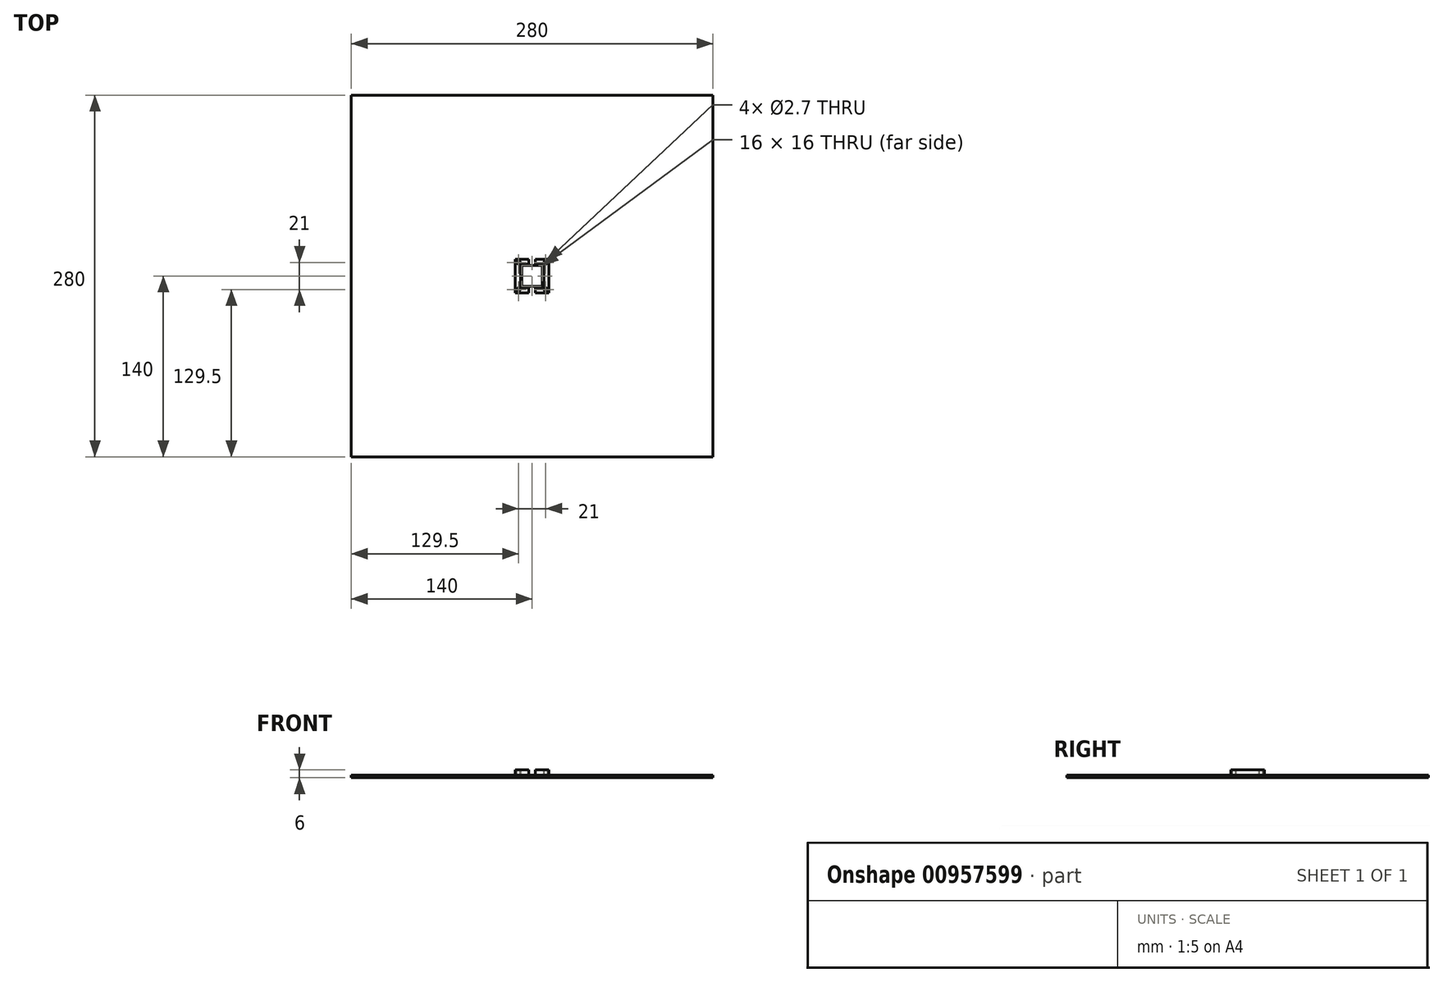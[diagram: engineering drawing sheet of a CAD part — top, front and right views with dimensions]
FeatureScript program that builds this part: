
annotation { "Feature Type Name" : "Feature", "Feature Type Description" : "" }
export const myFeature = defineFeature(function(context is Context, id is Id, definition is map)
    precondition{}
    {
        {
            var Q0;
            Q0=qCreatedBy(makeId("Top.planeOp"),FACE);
            var sketch = newSketch(context, id + "F0", { "sketchPlane" : qUnion([Q0])});
            skLineSegment(sketch, "E0.bottom", {"start": v(25, 25) * mm, "end": v(-25, 25) * mm});
            skLineSegment(sketch, "E0.top", {"start": v(25, -25) * mm, "end": v(-25, -25) * mm});
            skLineSegment(sketch, "E0.left", {"start": v(25, 25) * mm, "end": v(25, -25) * mm});
            skLineSegment(sketch, "E0.right", {"start": v(-25, 25) * mm, "end": v(-25, -25) * mm});
            skPoint(sketch, "E0.middle", {"position": v(0, 0) * mm});
            skLineSegment(sketch, "E1.bottom", {"start": v(140, -140) * mm, "end": v(-140, -140) * mm});
            skLineSegment(sketch, "E1.top", {"start": v(140, 140) * mm, "end": v(-140, 140) * mm});
            skLineSegment(sketch, "E1.left", {"start": v(140, -140) * mm, "end": v(140, 140) * mm});
            skLineSegment(sketch, "E1.right", {"start": v(-140, -140) * mm, "end": v(-140, 140) * mm});
            skSolve(sketch);
        }
        {
            var Q0;
            Q0=makeQuery(id+"F0.imprint","IMPRINT",FACE,{"disambiguationData":[TD([[makeQuery(id+"F0.imprint","IMPRINT",EDGE,{"derivedFrom":sQuery(id+"F0.wireOp",EDGE,"E0.bottom")}),-1.0]])]});
            extrude(context, id + "F1", {"entities" : qUnion([Q0]), "depth" : 18 * mm, "offsetDistance" : 25 * mm});
        }
        {
            var Q0;
            Q0=makeQuery(id+"F0.imprint","IMPRINT",FACE,{"disambiguationData":[TD([[makeQuery(id+"F0.imprint","IMPRINT",EDGE,{"derivedFrom":sQuery(id+"F0.wireOp",EDGE,"E0.bottom")}),-1.0]])]});
            var Q1;
            Q1=makeQuery(id+"F0.imprint","IMPRINT",FACE,{"disambiguationData":[TD([[makeQuery(id+"F0.imprint","IMPRINT",EDGE,{"derivedFrom":sQuery(id+"F0.wireOp",EDGE,"E0.bottom")}),1.0]])]});
            extrude(context, id + "F2", {"entities" : qUnion([Q0, Q1]), "operationType" : NewBodyOperationType.ADD, "oppositeDirection" : true, "depth" : 2 * mm, "offsetDistance" : 25 * mm});
        }
        {
            var Q0;
            {var subQ0=sQuery(id+"F0.wireOp",EDGE,"E1.left");Q0=makeQuery(id+"F2.boolean.opBoolean","MERGE",FACE,{"derivedFrom":[makeQuery(id+"F1.opExtrude","SWEPT_FACE",FACE,{"disambiguationData":[OSD([subQ0])]}),makeQuery(id+"F2.opExtrude","SWEPT_FACE",FACE,{"disambiguationData":[OSD([subQ0])]})]});}
            var sketch = newSketch(context, id + "F3", { "sketchPlane" : qUnion([Q0])});
            skLineSegment(sketch, "E2.bottom", {"start": v(-7.98, 6) * mm, "end": v(8.02, 6) * mm});
            skLineSegment(sketch, "E2.top", {"start": v(-7.98, 0) * mm, "end": v(8.02, 0) * mm});
            skLineSegment(sketch, "E2.left", {"start": v(-7.98, 6) * mm, "end": v(-7.98, 0) * mm});
            skLineSegment(sketch, "E2.right", {"start": v(8.02, 6) * mm, "end": v(8.02, 0) * mm});
            skLineSegment(sketch, "E3", {"start": v(-7.98, -2) * mm, "end": v(-7.98, 8) * mm, "construction": true});
            skLineSegment(sketch, "E4", {"start": v(8.02, -2) * mm, "end": v(8.02, 8) * mm, "construction": true});
            skLineSegment(sketch, "E5", {"start": v(-140, 6) * mm, "end": v(-7.98, 6) * mm, "construction": true});
            skLineSegment(sketch, "E6", {"start": v(8.02, 6) * mm, "end": v(140, 6) * mm, "construction": true});
            skSolve(sketch);
        }
        {
            var Q0;
            Q0=makeQuery(id+"F3.imprint","IMPRINT",FACE,{"disambiguationData":[TD([[makeQuery(id+"F3.imprint","IMPRINT",EDGE,{"derivedFrom":sQuery(id+"F3.wireOp",EDGE,"E2.bottom")}),-1.0]])]});
            extrude(context, id + "F4", {"entities" : qUnion([Q0]), "operationType" : NewBodyOperationType.REMOVE, "endBound" : BoundingType.UP_TO_NEXT, "oppositeDirection" : true, "depth" : 25 * mm, "offsetDistance" : 25 * mm});
        }
        {
            var Q0;
            Q0=makeQuery(id+"F1.opExtrude","CAP_FACE",FACE,{"disambiguationData":[OSD([sQuery(id+"F0.wireOp",EDGE,"E0.bottom"),sQuery(id+"F0.wireOp",EDGE,"E0.top"),sQuery(id+"F0.wireOp",EDGE,"E0.left"),sQuery(id+"F0.wireOp",EDGE,"E0.right"),sQuery(id+"F0.wireOp",EDGE,"E1.bottom"),sQuery(id+"F0.wireOp",EDGE,"E1.top"),sQuery(id+"F0.wireOp",EDGE,"E1.left"),sQuery(id+"F0.wireOp",EDGE,"E1.right")])],"isStart":false});
            var sketch = newSketch(context, id + "F5", { "sketchPlane" : qUnion([Q0])});
            skLineSegment(sketch, "E7.bottom", {"start": v(-140, -140) * mm, "end": v(140, -140) * mm});
            skLineSegment(sketch, "E7.top", {"start": v(-140, 140) * mm, "end": v(140, 140) * mm});
            skLineSegment(sketch, "E7.left", {"start": v(-140, -140) * mm, "end": v(-140, 140) * mm});
            skLineSegment(sketch, "E7.right", {"start": v(140, -140) * mm, "end": v(140, 140) * mm});
            skLineSegment(sketch, "E8.bottom", {"start": v(8, -8) * mm, "end": v(-8, -8) * mm});
            skLineSegment(sketch, "E8.top", {"start": v(8, 8) * mm, "end": v(-8, 8) * mm});
            skLineSegment(sketch, "E8.left", {"start": v(8, -8) * mm, "end": v(8, 8) * mm});
            skLineSegment(sketch, "E8.right", {"start": v(-8, -8) * mm, "end": v(-8, 8) * mm});
            skPoint(sketch, "E8.middle", {"position": v(0, 0) * mm});
            skSolve(sketch);
        }
        {
            var Q0;
            Q0=makeQuery(id+"F5.imprint","IMPRINT",FACE,{"disambiguationData":[TD([[makeQuery(id+"F5.imprint","IMPRINT",EDGE,{"derivedFrom":sQuery(id+"F5.wireOp",EDGE,"E8.bottom")}),1.0]])]});
            var Q1;
            Q1=makeQuery(id+"F5.imprint","IMPRINT",FACE,{"disambiguationData":[TD([[makeQuery(id+"F5.imprint","IMPRINT",EDGE,{"derivedFrom":sQuery(id+"F5.wireOp",EDGE,"E7.bottom")}),-1.0]])]});
            extrude(context, id + "F6", {"entities" : qUnion([Q0, Q1]), "depth" : 2 * mm, "offsetDistance" : 25 * mm});
        }
        {
            var Q0;
            Q0=makeQuery(id+"F6.opExtrude","CAP_FACE",FACE,{"disambiguationData":[OSD([sQuery(id+"F5.wireOp",EDGE,"E7.bottom"),sQuery(id+"F5.wireOp",EDGE,"E7.top"),sQuery(id+"F5.wireOp",EDGE,"E7.left"),sQuery(id+"F5.wireOp",EDGE,"E7.right"),sQuery(id+"F5.wireOp",EDGE,"E8.bottom"),sQuery(id+"F5.wireOp",EDGE,"E8.top"),sQuery(id+"F5.wireOp",EDGE,"E8.left"),sQuery(id+"F5.wireOp",EDGE,"E8.right")])],"isStart":false});
            var sketch = newSketch(context, id + "F7", { "sketchPlane" : qUnion([Q0])});
            skLineSegment(sketch, "E9.bottom", {"start": v(-9, 9) * mm, "end": v(9, 9) * mm});
            skLineSegment(sketch, "E9.top", {"start": v(-9, -9) * mm, "end": v(9, -9) * mm});
            skLineSegment(sketch, "E9.left", {"start": v(-9, 9) * mm, "end": v(-9, -9) * mm});
            skLineSegment(sketch, "E9.right", {"start": v(9, 9) * mm, "end": v(9, -9) * mm});
            skPoint(sketch, "E9.middle", {"position": v(0, 0) * mm});
            skLineSegment(sketch, "E10.bottom", {"start": v(13, 13) * mm, "end": v(-13, 13) * mm});
            skLineSegment(sketch, "E10.top", {"start": v(13, -13) * mm, "end": v(-13, -13) * mm});
            skLineSegment(sketch, "E10.left", {"start": v(13, 13) * mm, "end": v(13, -13) * mm});
            skLineSegment(sketch, "E10.right", {"start": v(-13, 13) * mm, "end": v(-13, -13) * mm});
            skSolve(sketch);
        }
        {
            var Q0;
            Q0=makeQuery(id+"F7.imprint","IMPRINT",FACE,{"disambiguationData":[TD([[makeQuery(id+"F7.imprint","IMPRINT",EDGE,{"derivedFrom":sQuery(id+"F7.wireOp",EDGE,"E9.bottom")}),1.0]])]});
            extrude(context, id + "F8", {"entities" : qUnion([Q0]), "operationType" : NewBodyOperationType.ADD, "depth" : 4 * mm, "offsetDistance" : 25 * mm});
        }
        {
            var Q0;
            Q0=makeQuery(id+"F8.opExtrude","CAP_FACE",FACE,{"disambiguationData":[OSD([sQuery(id+"F7.wireOp",EDGE,"E9.bottom"),sQuery(id+"F7.wireOp",EDGE,"E9.top"),sQuery(id+"F7.wireOp",EDGE,"E9.left"),sQuery(id+"F7.wireOp",EDGE,"E9.right"),sQuery(id+"F7.wireOp",EDGE,"E10.bottom"),sQuery(id+"F7.wireOp",EDGE,"E10.top"),sQuery(id+"F7.wireOp",EDGE,"E10.left"),sQuery(id+"F7.wireOp",EDGE,"E10.right")])],"isStart":false});
            var sketch = newSketch(context, id + "F9", { "sketchPlane" : qUnion([Q0])});
            skLineSegment(sketch, "E11", {"start": v(-2.5, 13) * mm, "end": v(-2.5, 9) * mm});
            skLineSegment(sketch, "E12.MirrorCS", {"start": v(2.5, 13) * mm, "end": v(2.5, 9) * mm});
            skLineSegment(sketch, "E13.MirrorCS", {"start": v(2.5, -13) * mm, "end": v(2.5, -9) * mm});
            skLineSegment(sketch, "E14.MirrorCS", {"start": v(-2.5, -13) * mm, "end": v(-2.5, -9) * mm});
            skLineSegment(sketch, "E15", {"start": v(-13, 13) * mm, "end": v(-9, 9) * mm, "construction": true});
            skPoint(sketch, "E16", {"position": v(-10.5, 10.5) * mm});
            skPoint(sketch, "E17.MirrorP", {"position": v(10.5, 10.5) * mm});
            skLineSegment(sketch, "E18.MirrorCS", {"start": v(13, 13) * mm, "end": v(9, 9) * mm, "construction": true});
            skLineSegment(sketch, "E19.MirrorCS", {"start": v(-13, -13) * mm, "end": v(-9, -9) * mm, "construction": true});
            skPoint(sketch, "E20.MirrorP", {"position": v(-10.5, -10.5) * mm});
            skLineSegment(sketch, "E21.MirrorCS", {"start": v(13, -13) * mm, "end": v(9, -9) * mm, "construction": true});
            skPoint(sketch, "E22.MirrorP", {"position": v(10.5, -10.5) * mm});
            skSolve(sketch);
        }
        {
            var Q0;
            Q0=sQuery(id+"F9.wireOp",VERTEX,"E16");
            var Q1;
            Q1=sQuery(id+"F9.wireOp",VERTEX,"E17.MirrorP");
            var Q2;
            Q2=sQuery(id+"F9.wireOp",VERTEX,"E20.MirrorP");
            var Q3;
            Q3=sQuery(id+"F9.wireOp",VERTEX,"E22.MirrorP");
            var Q4;
            Q4=makeQuery(id+"F6.opExtrude","SWEPT_BODY",BODY,{"disambiguationData":[OSD([sQuery(id+"F5.wireOp",EDGE,"E7.bottom"),sQuery(id+"F5.wireOp",EDGE,"E7.top"),sQuery(id+"F5.wireOp",EDGE,"E7.left"),sQuery(id+"F5.wireOp",EDGE,"E7.right"),sQuery(id+"F5.wireOp",EDGE,"E8.bottom"),sQuery(id+"F5.wireOp",EDGE,"E8.top"),sQuery(id+"F5.wireOp",EDGE,"E8.left"),sQuery(id+"F5.wireOp",EDGE,"E8.right")])]});
            hole(context, id + "F10", {"style" : HoleStyle.SIMPLE, "endStyle" : HoleEndStyle.BLIND, "standardTappedOrClearance" : lookupTablePath({ "standard" : "ISO", "engagement" : "50%", "pitch" : "0.5 mm", "size" : "M3", "type" : "Tapped" }), "standardBlindInLast" : lookupTablePath({ "standard" : "ISO", "fit" : "Normal", "engagement" : "50%", "pitch" : "0.5 mm", "size" : "M3", "type" : "Clearance & tapped" }), "holeDiameter" : 2.7 * mm, "majorDiameter" : 3 * mm, "showTappedDepth" : true, "holeDepth" : 8 * mm, "isTappedThrough" : true, "tappedDepth" : 6.5 * mm, "tapClearance" : 3, "locations" : qUnion([Q0, Q1, Q2, Q3]), "scope" : qUnion([Q4])});
        }
        {
            var Q0;
            {var subQ0=sQuery(id+"F9.wireOp",EDGE,"E11");Q0=makeQuery(id+"F9.imprint","IMPRINT",FACE,{"disambiguationData":[TD([[makeQuery(id+"F9.imprint","IMPRINT",EDGE,{"derivedFrom":subQ0}),1.0]])]});}
            var Q1;
            {var subQ0=sQuery(id+"F9.wireOp",EDGE,"E13.MirrorCS");Q1=makeQuery(id+"F9.imprint","IMPRINT",FACE,{"disambiguationData":[TD([[makeQuery(id+"F9.imprint","IMPRINT",EDGE,{"derivedFrom":subQ0}),1.0]])]});}
            var Q2;
            {var subQ0=sQuery(id+"F5.wireOp",EDGE,"E7.left");var subQ1=sQuery(id+"F5.wireOp",EDGE,"E7.top");var subQ2=sQuery(id+"F5.wireOp",EDGE,"E7.right");var subQ3=sQuery(id+"F5.wireOp",EDGE,"E7.bottom");Q2=makeQuery(id+"F8.boolean.opBoolean","SPLIT",FACE,{"disambiguationData":[TD([makeQuery(id+"F6.opExtrude","SWEPT_FACE",FACE,{"disambiguationData":[OSD([subQ3])]})])],"derivedFrom":makeQuery(id+"F6.opExtrude","CAP_FACE",FACE,{"disambiguationData":[OSD([subQ3,subQ1,subQ0,subQ2,sQuery(id+"F5.wireOp",EDGE,"E8.bottom"),sQuery(id+"F5.wireOp",EDGE,"E8.top"),sQuery(id+"F5.wireOp",EDGE,"E8.left"),sQuery(id+"F5.wireOp",EDGE,"E8.right")])],"isStart":false})});}
            extrude(context, id + "F11", {"entities" : qUnion([Q0, Q1]), "operationType" : NewBodyOperationType.REMOVE, "endBound" : BoundingType.UP_TO_SURFACE, "oppositeDirection" : true, "depth" : 25 * mm, "endBoundEntityFace" : qUnion([Q2]), "offsetDistance" : 25 * mm});
        }
        {
            var Q0;
            Q0=makeQuery(id+"F1.opExtrude","SWEPT_BODY",BODY,{"disambiguationData":[OSD([sQuery(id+"F0.wireOp",EDGE,"E0.bottom"),sQuery(id+"F0.wireOp",EDGE,"E0.top"),sQuery(id+"F0.wireOp",EDGE,"E0.left"),sQuery(id+"F0.wireOp",EDGE,"E0.right"),sQuery(id+"F0.wireOp",EDGE,"E1.bottom"),sQuery(id+"F0.wireOp",EDGE,"E1.top"),sQuery(id+"F0.wireOp",EDGE,"E1.left"),sQuery(id+"F0.wireOp",EDGE,"E1.right")])]});
            deleteBodies(context, id + "F12", {"entities" : qUnion([Q0])});
        }
    });
